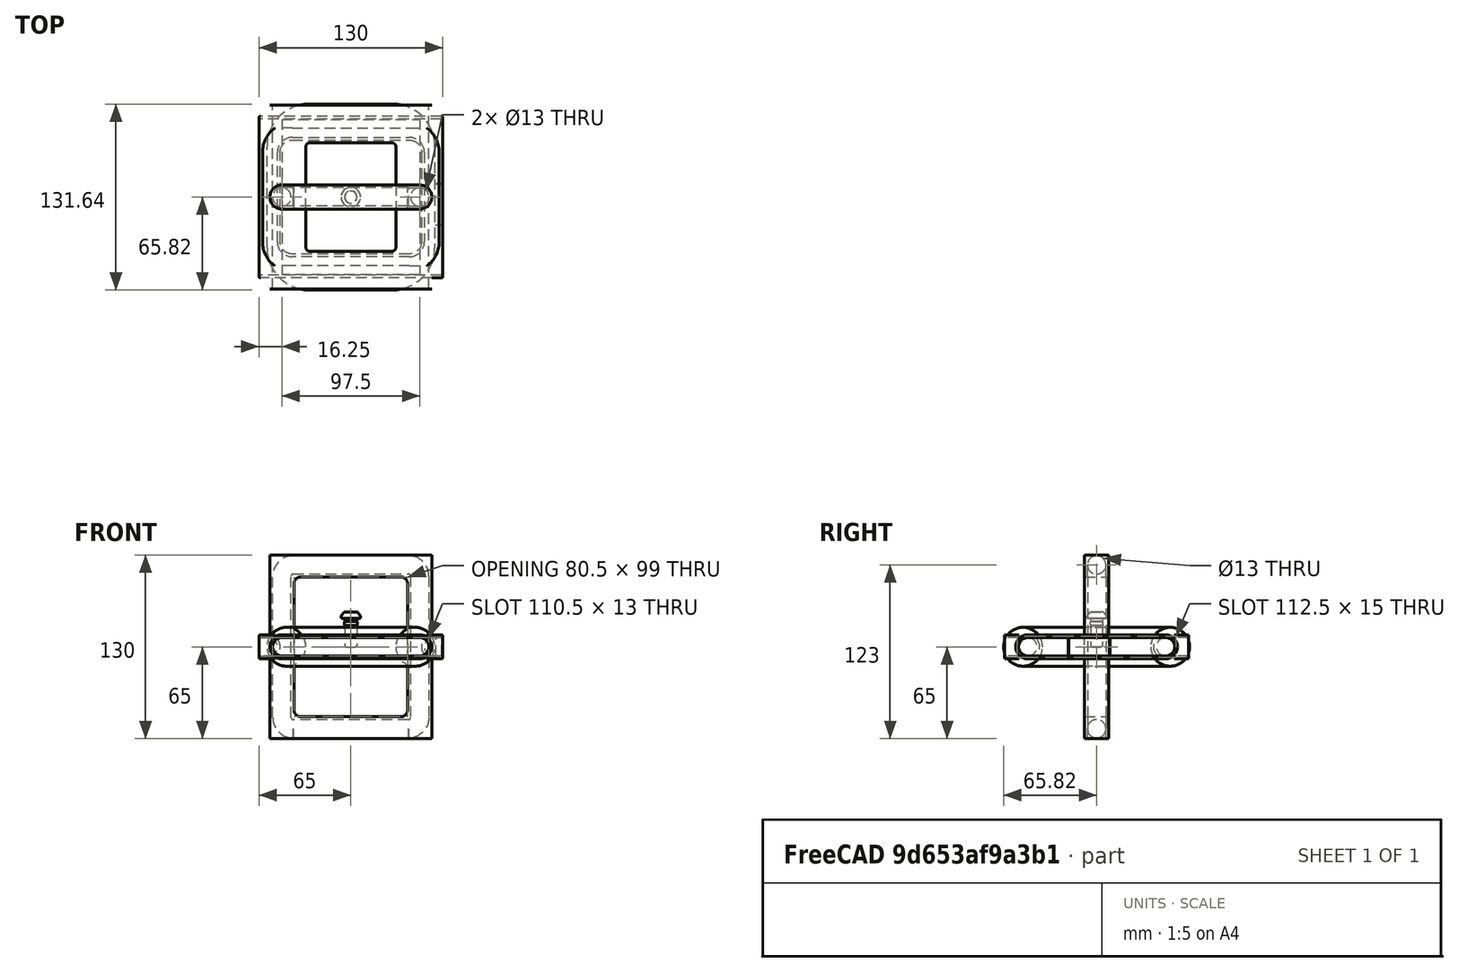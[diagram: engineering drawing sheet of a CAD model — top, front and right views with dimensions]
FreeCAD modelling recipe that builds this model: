
FCSTD DOCUMENT  (FreeCAD 0.19R24291 (Git))
Label: Cooler
License: All rights reserved
LicenseURL: http://en.wikipedia.org/wiki/All_rights_reserved
objects: Sketcher::SketchObject×23, PartDesign::Body×6, PartDesign::Pocket×5, PartDesign::Fillet×5, PartDesign::Pad×4, PartDesign::AdditivePipe×2, PartDesign::SubtractivePipe×1, PartDesign::Boolean×1, PartDesign::Revolution×1
note: 66 computed .brp shape members not serialized (recipe doc carries the construction recipe); baked Part::Feature solids carry a one-line shape summary decoded from their .brp

FEATURE [Sketcher::SketchObject] Sketch
  FullyConstrained = true
  MapMode = 5
  Support = -> [XY_Plane]
  sketch-geometry (6):
    g0: ArcOfCircle CenterX=-48.75 CenterY=-2e-16 CenterZ=0 NormalX=0 NormalY=0 NormalZ=1 AngleXU=0 Radius=8.5 StartAngle=1.5708 EndAngle=4.71239
    g1: ArcOfCircle CenterX=48.75 CenterY=2e-16 CenterZ=0 NormalX=0 NormalY=0 NormalZ=1 AngleXU=0 Radius=8.5 StartAngle=4.71239 EndAngle=7.85398
    g2: LineSegment StartX=-48.75 StartY=-8.5 StartZ=0 EndX=48.75 EndY=-8.5 EndZ=0
    g3: LineSegment StartX=-48.75 StartY=8.5 StartZ=0 EndX=48.75 EndY=8.5 EndZ=0
    g4: LineSegment StartX=48.75 StartY=2e-16 StartZ=0 EndX=57.25 EndY=2e-16 EndZ=0
    g5: LineSegment StartX=-48.75 StartY=-2e-16 StartZ=0 EndX=-57.25 EndY=-2e-16 EndZ=0
  constraints (15):
    c: Tangent(g0,g3) = 1.5708
    c: Tangent(g0,g2) = -1.5708
    c: Tangent(g2,g1) = -1.5708
    c: Tangent(g3,g1) = 1.5708
    c: Horizontal(g2)
    c: Equal(g0,g1)
    c: DistanceY(g0,g0) = 17
    c: Symmetric(g0,g1,g-1)
    c: Coincident(g4,g1)
    c: PointOnObject(g4,g1)
    c: Horizontal(g4)
    c: Coincident(g5,g0)
    c: PointOnObject(g5,g0)
    c: Horizontal(g5)
    c: DistanceX(g5,g4) = 114.5
FEATURE [PartDesign::Pad] Pad
  Direction = (1,1,1)
  Length = 130
  Length2 = 100
  Midplane = true
  Profile = -> Sketch
  Type = 0
FEATURE [Sketcher::SketchObject] Sketch001
  FullyConstrained = true
  MapMode = 5
  Placement = pos=(0,-8.5,0) rot=(1,0,0;1.5708rad)
  Support = -> [Pad]
  sketch-geometry (10):
    g0: LineSegment StartX=-35.25 StartY=49.5 StartZ=0 EndX=35.25 EndY=49.5 EndZ=0
    g1: LineSegment StartX=40.25 StartY=44.5 StartZ=0 EndX=40.25 EndY=-44.5 EndZ=0
    g2: LineSegment StartX=35.25 StartY=-49.5 StartZ=0 EndX=-35.25 EndY=-49.5 EndZ=0
    g3: LineSegment StartX=-40.25 StartY=-44.5 StartZ=0 EndX=-40.25 EndY=44.5 EndZ=0
    g4: LineSegment StartX=-57.25 StartY=0 StartZ=0 EndX=57.25 EndY=0 EndZ=0
    g5: LineSegment StartX=0 StartY=65 StartZ=0 EndX=0 EndY=-65 EndZ=0
    g6: ArcOfCircle CenterX=-35.25 CenterY=44.5 CenterZ=0 NormalX=0 NormalY=0 NormalZ=1 AngleXU=0 Radius=5 StartAngle=1.5708 EndAngle=3.14159
    g7: ArcOfCircle CenterX=-35.25 CenterY=-44.5 CenterZ=0 NormalX=0 NormalY=0 NormalZ=1 AngleXU=0 Radius=5 StartAngle=3.14159 EndAngle=4.71239
    g8: ArcOfCircle CenterX=35.25 CenterY=-44.5 CenterZ=0 NormalX=0 NormalY=0 NormalZ=1 AngleXU=0 Radius=5 StartAngle=4.71239 EndAngle=6.28319
    g9: ArcOfCircle CenterX=35.25 CenterY=44.5 CenterZ=0 NormalX=0 NormalY=0 NormalZ=1 AngleXU=0 Radius=5 StartAngle=0 EndAngle=1.5708
  constraints (25):
    c: Horizontal(g0)
    c: Horizontal(g2)
    c: Vertical(g1)
    c: Vertical(g3)
    c: PointOnObject(g4,g-1)
    c: DistanceX(g4,g4) = 114.5
    c: Symmetric(g4,g4,g-1)
    c: PointOnObject(g5,g-2)
    c: DistanceY(g5,g5) = 130
    c: Symmetric(g5,g5,g-1)
    c: Tangent(g0,g6) = 1.5708
    c: Tangent(g3,g6) = 1.5708
    c: Tangent(g3,g7) = 1.5708
    c: Tangent(g2,g7) = 1.5708
    c: Tangent(g1,g8) = 1.5708
    c: Tangent(g2,g8) = 1.5708
    c: Tangent(g1,g9) = 1.5708
    c: Tangent(g0,g9) = 1.5708
    c: DistanceY(g0,g5) = 15.5
    c: DistanceX(g1,g4) = 17
    c: Symmetric(g6,g8,g-1)
    c: Equal(g9,g6)
    c: Equal(g6,g7)
    c: Equal(g7,g8)
    c: Radius(g7) = 5
FEATURE [PartDesign::Pocket] Pocket
  BaseFeature = -> Pad
  Length = 5
  Length2 = 100
  Profile = -> Sketch001
  Type = 1
FEATURE [Sketcher::SketchObject] Sketch002
  ExternalGeometry = -> [Pocket]
  FullyConstrained = true
  MapMode = 5
  Support = -> [XY_Plane]
  sketch-geometry (4):
    g0: LineSegment StartX=-48.75 StartY=-2e-16 StartZ=0 EndX=48.75 EndY=8.11e-14 EndZ=0
    g1: Circle CenterX=48.75 CenterY=8.11e-14 CenterZ=0 NormalX=0 NormalY=0 NormalZ=1 AngleXU=0 Radius=6.5
    g2: Circle CenterX=-48.75 CenterY=-2e-16 CenterZ=0 NormalX=0 NormalY=0 NormalZ=1 AngleXU=0 Radius=6.5
    g3: LineSegment StartX=-48.75 StartY=-6.5 StartZ=0 EndX=-48.75 EndY=-8.5 EndZ=0
  constraints (9):
    c: Coincident(g0,g-3)
    c: Symmetric(g0,g0,g-1)
    c: Coincident(g1,g0)
    c: Coincident(g2,g0)
    c: Equal(g1,g2)
    c: PointOnObject(g3,g2)
    c: Coincident(g3,g-3)
    c: Vertical(g3)
    c: DistanceY(g3,g3) = 2
FEATURE [Sketcher::SketchObject] Sketch004
  ExternalGeometry = -> [Pocket]
  FullyConstrained = true
  MapMode = 5
  Placement = pos=(0,0,-65) rot=(1,0,0;3.14159rad)
  Support = -> [Pocket]
  sketch-geometry (4):
    g0: ArcOfCircle CenterX=-48.75 CenterY=4.25e-14 CenterZ=0 NormalX=0 NormalY=0 NormalZ=1 AngleXU=0 Radius=6.5 StartAngle=1.5708 EndAngle=4.71239
    g1: ArcOfCircle CenterX=48.75 CenterY=-4.25e-14 CenterZ=0 NormalX=0 NormalY=0 NormalZ=1 AngleXU=0 Radius=6.5 StartAngle=4.71239 EndAngle=7.85398
    g2: LineSegment StartX=-48.75 StartY=-6.5 StartZ=0 EndX=48.75 EndY=-6.5 EndZ=0
    g3: LineSegment StartX=-48.75 StartY=6.5 StartZ=0 EndX=48.75 EndY=6.5 EndZ=0
  constraints (11):
    c: Tangent(g0,g3) = 1.5708
    c: Tangent(g0,g2) = -1.5708
    c: Tangent(g2,g1) = -1.5708
    c: Tangent(g3,g1) = 1.5708
    c: Horizontal(g2)
    c: Symmetric(g1,g0,g-1)
    c: DistanceY(g-3,g0) = 2
    c: Horizontal(g3)
    c: Vertical(g-3,g0)
    c: DistanceY(g1,g1) = 13
    c: DistanceY(g-3,g-4) = 17
FEATURE [Sketcher::SketchObject] Sketch005
  FullyConstrained = false
  MapMode = 5
  Placement = pos=(0,0,0) rot=(1,0,0;1.5708rad)
  Support = -> [XZ_Plane001]
  sketch-geometry (1):
    g0: Circle CenterX=-45.5792 CenterY=0 CenterZ=0 NormalX=0 NormalY=0 NormalZ=1 AngleXU=0 Radius=13.7562
  constraints (1):
    c: PointOnObject(g0,g-1)
FEATURE [Sketcher::SketchObject] Sketch006
  FullyConstrained = false
  MapMode = 5
  Support = -> [XY_Plane001]
  sketch-geometry (8):
    g0: LineSegment StartX=-29.3214 StartY=54.1567 StartZ=0 EndX=29.3214 EndY=54.1567 EndZ=0
    g1: LineSegment StartX=47.6711 StartY=35.807 StartZ=0 EndX=47.6711 EndY=-35.807 EndZ=0
    g2: LineSegment StartX=29.3214 StartY=-54.1567 StartZ=0 EndX=-29.3214 EndY=-54.1567 EndZ=0
    g3: LineSegment StartX=-47.6711 StartY=-35.807 StartZ=0 EndX=-47.6711 EndY=35.807 EndZ=0
    g4: ArcOfCircle CenterX=-29.3214 CenterY=35.807 CenterZ=0 NormalX=0 NormalY=0 NormalZ=1 AngleXU=0 Radius=18.3497 StartAngle=1.5708 EndAngle=3.14159
    g5: ArcOfCircle CenterX=-29.3214 CenterY=-35.807 CenterZ=0 NormalX=0 NormalY=0 NormalZ=1 AngleXU=0 Radius=18.3497 StartAngle=3.14159 EndAngle=4.71239
    g6: ArcOfCircle CenterX=29.3214 CenterY=-35.807 CenterZ=0 NormalX=0 NormalY=0 NormalZ=1 AngleXU=0 Radius=18.3497 StartAngle=4.71239 EndAngle=6.28319
    g7: ArcOfCircle CenterX=29.3214 CenterY=35.807 CenterZ=0 NormalX=0 NormalY=0 NormalZ=1 AngleXU=0 Radius=18.3497 StartAngle=0 EndAngle=1.5708
  constraints (16):
    c: Horizontal(g0)
    c: Horizontal(g2)
    c: Vertical(g1)
    c: Vertical(g3)
    c: Tangent(g0,g4) = 1.5708
    c: Tangent(g3,g4) = 1.5708
    c: Tangent(g3,g5) = 1.5708
    c: Tangent(g2,g5) = 1.5708
    c: Tangent(g2,g6) = 1.5708
    c: Tangent(g1,g6) = 1.5708
    c: Tangent(g1,g7) = 1.5708
    c: Tangent(g0,g7) = 1.5708
    c: Equal(g7,g4)
    c: Equal(g4,g5)
    c: Equal(g5,g6)
    c: Symmetric(g4,g6,g-1)
FEATURE [PartDesign::AdditivePipe] AdditivePipe
  AuxilleryCurvelinear = true
  AuxillerySpineTangent = false
  Binormal = (0,0,0)
  Mode = 0
  Placement = pos=(0,0,0) rot=(1,0,0;1.5708rad)
  Profile = -> Sketch005
  Spine = -> Sketch006
  SpineTangent = false
  Transformation = 0
  Transition = 0
FEATURE [PartDesign::Body] Body001
  Group = -> [Sketch005,Sketch006,AdditivePipe]
  Origin = -> Origin001
  Tip = -> AdditivePipe
FEATURE [Sketcher::SketchObject] Sketch007
  ExternalGeometry = -> [Pocket]
  FullyConstrained = true
  MapMode = 5
  Support = -> [XY_Plane]
  sketch-geometry (2):
    g0: Circle CenterX=-48.75 CenterY=0 CenterZ=0 NormalX=0 NormalY=0 NormalZ=1 AngleXU=0 Radius=6.5
    g1: LineSegment StartX=-57.25 StartY=0 StartZ=0 EndX=-55.25 EndY=0 EndZ=0
  constraints (8):
    c: Radius(g0) = 6.5
    c: PointOnObject(g0,g-1)
    c: PointOnObject(g1,g-3)
    c: PointOnObject(g1,g0)
    c: Horizontal(g1)
    c: PointOnObject(g1,g-1)
    c: DistanceX(g1,g1) = 2
    c: DistanceX(g1,g0) = 8.5
FEATURE [Sketcher::SketchObject] Sketch008
  ExternalGeometry = -> [Pocket]
  FullyConstrained = true
  MapMode = 5
  Placement = pos=(0,0,0) rot=(1,0,0;1.5708rad)
  Support = -> [XZ_Plane]
  sketch-geometry (8):
    g0: LineSegment StartX=-40.75 StartY=58 StartZ=0 EndX=40.75 EndY=58 EndZ=0
    g1: LineSegment StartX=48.75 StartY=50 StartZ=0 EndX=48.75 EndY=-50 EndZ=0
    g2: LineSegment StartX=40.75 StartY=-58 StartZ=0 EndX=-40.75 EndY=-58 EndZ=0
    g3: LineSegment StartX=-48.75 StartY=-50 StartZ=0 EndX=-48.75 EndY=50 EndZ=0
    g4: ArcOfCircle CenterX=-40.75 CenterY=-50 CenterZ=0 NormalX=0 NormalY=0 NormalZ=1 AngleXU=0 Radius=8 StartAngle=3.14159 EndAngle=4.71239
    g5: ArcOfCircle CenterX=40.75 CenterY=-50 CenterZ=0 NormalX=0 NormalY=0 NormalZ=1 AngleXU=0 Radius=8 StartAngle=4.71239 EndAngle=6.28319
    g6: ArcOfCircle CenterX=40.75 CenterY=50 CenterZ=0 NormalX=0 NormalY=0 NormalZ=1 AngleXU=0 Radius=8 StartAngle=0 EndAngle=1.5708
    g7: ArcOfCircle CenterX=-40.75 CenterY=50 CenterZ=0 NormalX=0 NormalY=0 NormalZ=1 AngleXU=0 Radius=8 StartAngle=1.5708 EndAngle=3.14159
  constraints (22):
    c: Horizontal(g0)
    c: Horizontal(g2)
    c: Vertical(g1)
    c: Vertical(g3)
    c: Tangent(g2,g4) = 1.5708
    c: Tangent(g3,g4) = 1.5708
    c: Tangent(g1,g5) = 1.5708
    c: Tangent(g2,g5) = 1.5708
    c: Tangent(g1,g6) = 1.5708
    c: Tangent(g0,g6) = 1.5708
    c: Tangent(g0,g7) = 1.5708
    c: Tangent(g3,g7) = 1.5708
    c: Equal(g7,g6)
    c: Equal(g6,g5)
    c: Equal(g5,g4)
    c: Symmetric(g7,g5,g-1)
    c: DistanceX(g-4,g-1) = 48.75
    c: DistanceY(g-5,g-4) = 15.5
    c: DistanceY(g-5,g0) = 8.5
    c: Radius(g6) = 8
    c: DistanceX(g-4,g-3) = 8.5
    c: Vertical(g3,g-4)
FEATURE [PartDesign::SubtractivePipe] SubtractivePipe
  AuxilleryCurvelinear = true
  AuxillerySpineTangent = false
  BaseFeature = -> Pocket
  Binormal = (0,0,0)
  Mode = 0
  Profile = -> Sketch007
  Spine = -> Sketch008
  SpineTangent = false
  Transformation = 0
  Transition = 1
FEATURE [Sketcher::SketchObject] Sketch003
  ExternalGeometry = -> [SubtractivePipe]
  FullyConstrained = true
  MapMode = 5
  Placement = pos=(0,0,0) rot=(0.57735,0.57735,0.57735;2.0944rad)
  Support = -> [YZ_Plane]
  sketch-geometry (4):
    g0: LineSegment StartX=-6.5 StartY=-65 StartZ=0 EndX=6.5 EndY=-65 EndZ=0
    g1: LineSegment StartX=-6.5 StartY=-65 StartZ=0 EndX=-6.5 EndY=-58 EndZ=0
    g2: LineSegment StartX=6.5 StartY=-65 StartZ=0 EndX=6.5 EndY=-58 EndZ=0
    g3: ArcOfCircle CenterX=3.48e-14 CenterY=-58 CenterZ=0 NormalX=0 NormalY=0 NormalZ=1 AngleXU=0 Radius=6.5 StartAngle=-1.07e-14 EndAngle=3.14159
  constraints (9):
    c: Symmetric(g0,g0,g-2)
    c: Coincident(g0,g1)
    c: Vertical(g1)
    c: Coincident(g0,g2)
    c: Tangent(g3,g2) = -1.5708
    c: Tangent(g1,g3) = 1.5708
    c: Radius(g3) = 6.5
    c: Coincident(g3,g-3)
    c: PointOnObject(g0,g-4)
FEATURE [Sketcher::SketchObject] Sketch009
  FullyConstrained = true
  MapMode = 5
  Placement = pos=(0,0,0) rot=(1,0,0;1.5708rad)
  Support = -> [XZ_Plane002]
  sketch-geometry (10):
    g0: ArcOfCircle CenterX=-48.75 CenterY=0 CenterZ=0 NormalX=0 NormalY=0 NormalZ=1 AngleXU=0 Radius=6.5 StartAngle=1.5708 EndAngle=4.71239
    g1: ArcOfCircle CenterX=48.75 CenterY=0 CenterZ=0 NormalX=0 NormalY=0 NormalZ=1 AngleXU=0 Radius=6.5 StartAngle=4.71239 EndAngle=7.85398
    g2: LineSegment StartX=-48.75 StartY=-6.5 StartZ=0 EndX=48.75 EndY=-6.5 EndZ=0
    g3: LineSegment StartX=-48.75 StartY=6.5 StartZ=0 EndX=48.75 EndY=6.5 EndZ=0
    g4: ArcOfCircle CenterX=-48.75 CenterY=0 CenterZ=0 NormalX=0 NormalY=0 NormalZ=1 AngleXU=0 Radius=8.5 StartAngle=1.5708 EndAngle=4.71239
    g5: ArcOfCircle CenterX=48.75 CenterY=0 CenterZ=0 NormalX=0 NormalY=0 NormalZ=1 AngleXU=0 Radius=8.5 StartAngle=4.71239 EndAngle=7.85398
    g6: LineSegment StartX=-48.75 StartY=-8.5 StartZ=0 EndX=48.75 EndY=-8.5 EndZ=0
    g7: LineSegment StartX=-48.75 StartY=8.5 StartZ=0 EndX=48.75 EndY=8.5 EndZ=0
    g8: LineSegment StartX=48.75 StartY=0 StartZ=0 EndX=57.25 EndY=0 EndZ=0
    g9: LineSegment StartX=-48.75 StartY=0 StartZ=0 EndX=-57.25 EndY=0 EndZ=0
  constraints (23):
    c: Tangent(g0,g3) = 1.5708
    c: Tangent(g0,g2) = -1.5708
    c: Tangent(g2,g1) = -1.5708
    c: Tangent(g3,g1) = 1.5708
    c: Horizontal(g2)
    c: Tangent(g4,g7) = 1.5708
    c: Tangent(g4,g6) = -1.5708
    c: Tangent(g6,g5) = -1.5708
    c: Tangent(g7,g5) = 1.5708
    c: Horizontal(g6)
    c: Coincident(g4,g0)
    c: Coincident(g1,g5)
    c: DistanceY(g1,g5) = 2
    c: Symmetric(g0,g1,g-2)
    c: PointOnObject(g0,g-1)
    c: Radius(g4) = 8.5
    c: Coincident(g8,g1)
    c: PointOnObject(g8,g-1)
    c: PointOnObject(g8,g5)
    c: Coincident(g9,g0)
    c: PointOnObject(g9,g-1)
    c: PointOnObject(g9,g4)
    c: DistanceX(g9,g8) = 114.5
FEATURE [Sketcher::SketchObject] Sketch010
  ExternalGeometry = -> [Sketch009]
  FullyConstrained = true
  MapMode = 5
  Placement = pos=(0,0,0) rot=(1,0,0;1.5708rad)
  Support = -> [XZ_Plane002]
  sketch-geometry (6):
    g0: Circle CenterX=-48.75 CenterY=0 CenterZ=0 NormalX=0 NormalY=0 NormalZ=1 AngleXU=0 Radius=8.5
    g1: Circle CenterX=-48.75 CenterY=0 CenterZ=0 NormalX=0 NormalY=0 NormalZ=1 AngleXU=0 Radius=6.5
    g2: LineSegment StartX=-55.25 StartY=0 StartZ=0 EndX=-57.25 EndY=0 EndZ=0
    g3: Circle CenterX=48.75 CenterY=0 CenterZ=0 NormalX=0 NormalY=0 NormalZ=1 AngleXU=0 Radius=6.5
    g4: Circle CenterX=48.75 CenterY=0 CenterZ=0 NormalX=0 NormalY=0 NormalZ=1 AngleXU=0 Radius=8.5
    g5: LineSegment StartX=55.25 StartY=0 StartZ=0 EndX=57.25 EndY=0 EndZ=0
  constraints (16):
    c: Coincident(g0,g-3)
    c: Coincident(g1,g0)
    c: PointOnObject(g2,g1)
    c: PointOnObject(g2,g0)
    c: Horizontal(g2)
    c: DistanceX(g2,g2) = 2
    c: PointOnObject(g2,g-1)
    c: Coincident(g4,g3)
    c: PointOnObject(g5,g3)
    c: PointOnObject(g5,g4)
    c: Horizontal(g5)
    c: Equal(g5,g2)
    c: Equal(g4,g0)
    c: Symmetric(g3,g0,g-1)
    c: PointOnObject(g5,g-1)
    c: Equal(g0,g-3)
FEATURE [PartDesign::Pad] Pad001
  Direction = (1,1,1)
  Length = 130
  Length2 = 100
  Midplane = true
  Placement = pos=(0,0,0) rot=(1,0,0;1.5708rad)
  Profile = -> Sketch009
  Type = 0
FEATURE [Sketcher::SketchObject] Sketch011
  ExternalGeometry = -> [Pad001]
  FullyConstrained = true
  MapMode = 5
  Placement = pos=(0,3.7e-15,8.5) rot=(0,0,1;3.14159rad)
  Support = -> [Pad001]
  sketch-geometry (4):
    g0: LineSegment StartX=-48.75 StartY=55 StartZ=0 EndX=48.75 EndY=55 EndZ=0
    g1: LineSegment StartX=48.75 StartY=55 StartZ=0 EndX=48.75 EndY=-55 EndZ=0
    g2: LineSegment StartX=48.75 StartY=-55 StartZ=0 EndX=-48.75 EndY=-55 EndZ=0
    g3: LineSegment StartX=-48.75 StartY=-55 StartZ=0 EndX=-48.75 EndY=55 EndZ=0
  constraints (11):
    c: Coincident(g0,g1)
    c: Coincident(g1,g2)
    c: Coincident(g2,g3)
    c: Coincident(g3,g0)
    c: Horizontal(g0)
    c: Vertical(g3)
    c: Symmetric(g2,g1,g-2)
    c: Symmetric(g0,g1,g-1)
    c: PointOnObject(g0,g-3)
    c: DistanceY(g2,g-1) = 55
    c: DistanceX(g0,g0) = 97.5
FEATURE [PartDesign::Pocket] Pocket003
  BaseFeature = -> Pad001
  Length = 5
  Length2 = 100
  Placement = pos=(0,0,0) rot=(1,0,0;1.5708rad)
  Profile = -> Sketch011
  Type = 1
FEATURE [Sketcher::SketchObject] Sketch012
  FullyConstrained = false
  MapMode = 2
  Placement = pos=(0,0,0) rot=(0.57735,0.57735,0.57735;2.0944rad)
  Support = -> [YZ_Plane002]
  sketch-geometry (8):
    g0: LineSegment StartX=-65 StartY=8.5 StartZ=0 EndX=-55 EndY=8.5 EndZ=0
    g1: LineSegment StartX=-65 StartY=-8.5 StartZ=0 EndX=-55 EndY=-8.5 EndZ=0
    g2: ArcOfCircle CenterX=-55 CenterY=6.95e-14 CenterZ=0 NormalX=0 NormalY=0 NormalZ=1 AngleXU=0 Radius=8.5 StartAngle=4.71239 EndAngle=7.85398
    g3: ArcOfCircle CenterX=-55 CenterY=6.95e-14 CenterZ=0 NormalX=0 NormalY=0 NormalZ=1 AngleXU=0 Radius=6.5 StartAngle=4.71239 EndAngle=7.85398
    g4: LineSegment StartX=-65 StartY=8.5 StartZ=0 EndX=-65 EndY=6.5 EndZ=0
    g5: LineSegment StartX=-65 StartY=6.5 StartZ=0 EndX=-55 EndY=6.5 EndZ=0
    g6: LineSegment StartX=-55 StartY=-6.5 StartZ=0 EndX=-65 EndY=-6.5 EndZ=0
    g7: LineSegment StartX=-65 StartY=-6.5 StartZ=0 EndX=-65 EndY=-8.5 EndZ=0
  constraints (16):
    c: Tangent(g2,g1) = -1.5708
    c: Tangent(g0,g2) = 1.5708
    c: Horizontal(g0)
    c: Horizontal(g1)
    c: Coincident(g3,g2)
    c: DistanceY(g3,g0) = 2
    c: Coincident(g0,g4)
    c: Vertical(g4)
    c: Coincident(g4,g5)
    c: Horizontal(g5)
    c: Tangent(g3,g6) = 1.5708
    c: Coincident(g6,g7)
    c: Coincident(g7,g1)
    c: Vertical(g7)
    c: Horizontal(g6)
    c: Tangent(g5,g3) = 1.5708
FEATURE [Sketcher::SketchObject] Sketch013
  FullyConstrained = false
  MapMode = 2
  Placement = pos=(0,0,0) rot=(0.57735,0.57735,0.57735;2.0944rad)
  Support = -> [YZ_Plane002]
  sketch-geometry (4):
    g0: ArcOfCircle CenterX=-55 CenterY=0 CenterZ=0 NormalX=0 NormalY=0 NormalZ=1 AngleXU=0 Radius=6.5 StartAngle=4.71239 EndAngle=7.85398
    g1: LineSegment StartX=-65 StartY=-6.5 StartZ=0 EndX=-65 EndY=6.5 EndZ=0
    g2: LineSegment StartX=-65 StartY=6.5 StartZ=0 EndX=-55 EndY=6.5 EndZ=0
    g3: LineSegment StartX=-55 StartY=-6.5 StartZ=0 EndX=-65 EndY=-6.5 EndZ=0
  constraints (9):
    c: Coincident(g1,g2)
    c: Horizontal(g2)
    c: Tangent(g0,g3) = 1.5708
    c: Horizontal(g3)
    c: Tangent(g2,g0) = 1.5708
    c: Coincident(g1,g3)
    c: DistanceX(g2,g2) = 10
    c: Radius(g0) = 6.5
    c: Symmetric(g1,g1,g-1)
FEATURE [Sketcher::SketchObject] Sketch014
  FullyConstrained = false
  MapMode = 5
  Placement = pos=(0,0,0) rot=(1,0,0;1.5708rad)
  Support = -> [XZ_Plane002]
  sketch-geometry (2):
    g0: Circle CenterX=-48.75 CenterY=1.443e-13 CenterZ=0 NormalX=0 NormalY=0 NormalZ=1 AngleXU=0 Radius=6.5
    g1: Circle CenterX=48.75 CenterY=1.443e-13 CenterZ=0 NormalX=0 NormalY=0 NormalZ=1 AngleXU=0 Radius=6.5
  constraints (2):
    c: Equal(g1,g0)
    c: Symmetric(g1,g0,g-2)
FEATURE [PartDesign::Body] Body002
  Group = -> [Sketch009,Sketch010,Pad001,Sketch011,Pocket003,Sketch012,Sketch013,Sketch014]
  Origin = -> Origin002
  Tip = -> Pocket003
FEATURE [PartDesign::Pocket] Pocket006
  BaseFeature = -> SubtractivePipe
  Length = 81.5
  Length2 = 100
  Midplane = true
  Profile = -> Sketch003
  Type = 0
FEATURE [PartDesign::Body] Body
  Group = -> [Sketch,Pad,Sketch001,Pocket,Sketch002,Sketch003,Sketch004,Sketch007,Sketch008,SubtractivePipe,Pocket006]
  Origin = -> Origin
  Tip = -> Pocket006
FEATURE [Sketcher::SketchObject] Sketch015
  FullyConstrained = true
  MapMode = 5
  Support = -> [XY_Plane003]
  sketch-geometry (8):
    g0: LineSegment StartX=-41.5 StartY=40.25 StartZ=0 EndX=41.5 EndY=40.25 EndZ=0
    g1: LineSegment StartX=50 StartY=31.75 StartZ=0 EndX=50 EndY=-31.75 EndZ=0
    g2: LineSegment StartX=41.5 StartY=-40.25 StartZ=0 EndX=-41.5 EndY=-40.25 EndZ=0
    g3: LineSegment StartX=-50 StartY=-31.75 StartZ=0 EndX=-50 EndY=31.75 EndZ=0
    g4: ArcOfCircle CenterX=-41.5 CenterY=-31.75 CenterZ=0 NormalX=0 NormalY=0 NormalZ=1 AngleXU=0 Radius=8.5 StartAngle=3.14159 EndAngle=4.71239
    g5: ArcOfCircle CenterX=41.5 CenterY=-31.75 CenterZ=0 NormalX=0 NormalY=0 NormalZ=1 AngleXU=0 Radius=8.5 StartAngle=4.71239 EndAngle=6.28319
    g6: ArcOfCircle CenterX=41.5 CenterY=31.75 CenterZ=0 NormalX=0 NormalY=0 NormalZ=1 AngleXU=0 Radius=8.5 StartAngle=0 EndAngle=1.5708
    g7: ArcOfCircle CenterX=-41.5 CenterY=31.75 CenterZ=0 NormalX=0 NormalY=0 NormalZ=1 AngleXU=0 Radius=8.5 StartAngle=1.5708 EndAngle=3.14159
  constraints (19):
    c: Horizontal(g0)
    c: Horizontal(g2)
    c: Vertical(g1)
    c: Vertical(g3)
    c: Tangent(g2,g4) = 1.5708
    c: Tangent(g3,g4) = 1.5708
    c: Tangent(g1,g5) = 1.5708
    c: Tangent(g2,g5) = 1.5708
    c: Tangent(g1,g6) = 1.5708
    c: Tangent(g0,g6) = 1.5708
    c: Tangent(g0,g7) = 1.5708
    c: Tangent(g3,g7) = 1.5708
    c: Equal(g7,g6)
    c: Equal(g6,g5)
    c: Equal(g5,g4)
    c: Symmetric(g7,g5,g-1)
    c: Radius(g6) = 8.5
    c: DistanceX(g3,g1) = 100
    c: DistanceY(g2,g0) = 80.5
FEATURE [Sketcher::SketchObject] Sketch016
  ExternalGeometry = -> [Pocket]
  FullyConstrained = true
  MapMode = 5
  Support = -> [XY_Plane003]
  sketch-geometry (2):
    g0: Circle CenterX=-48.75 CenterY=0 CenterZ=0 NormalX=0 NormalY=0 NormalZ=1 AngleXU=0 Radius=6.5
    g1: LineSegment StartX=-57.25 StartY=0 StartZ=0 EndX=-55.25 EndY=0 EndZ=0
  constraints (8):
    c: Radius(g0) = 6.5
    c: PointOnObject(g0,g-1)
    c: PointOnObject(g1,g-3)
    c: PointOnObject(g1,g0)
    c: Horizontal(g1)
    c: PointOnObject(g1,g-1)
    c: DistanceX(g1,g1) = 2
    c: DistanceX(g1,g0) = 8.5
FEATURE [Sketcher::SketchObject] Sketch017
  ExternalGeometry = -> [Sketch015]
  FullyConstrained = true
  MapMode = 2
  Placement = pos=(0,0,0) rot=(0.57735,0.57735,0.57735;2.0944rad)
  Support = -> [YZ_Plane003]
  sketch-geometry (9):
    g0: LineSegment StartX=-52.75 StartY=8.5 StartZ=0 EndX=-48.75 EndY=8.5 EndZ=0
    g1: LineSegment StartX=-52.75 StartY=-8.5 StartZ=0 EndX=-48.75 EndY=-8.5 EndZ=0
    g2: ArcOfCircle CenterX=-48.75 CenterY=0 CenterZ=0 NormalX=0 NormalY=0 NormalZ=1 AngleXU=0 Radius=8.5 StartAngle=4.71239 EndAngle=7.85398
    g3: ArcOfCircle CenterX=-48.75 CenterY=0 CenterZ=0 NormalX=0 NormalY=0 NormalZ=1 AngleXU=0 Radius=6.5 StartAngle=4.71239 EndAngle=7.85398
    g4: LineSegment StartX=-52.75 StartY=8.5 StartZ=0 EndX=-52.75 EndY=6.5 EndZ=0
    g5: LineSegment StartX=-52.75 StartY=6.5 StartZ=0 EndX=-48.75 EndY=6.5 EndZ=0
    g6: LineSegment StartX=-48.75 StartY=-6.5 StartZ=0 EndX=-52.75 EndY=-6.5 EndZ=0
    g7: LineSegment StartX=-52.75 StartY=-6.5 StartZ=0 EndX=-52.75 EndY=-8.5 EndZ=0
    g8: GeomPoint X=-40.25 Y=-1.12e-14 Z=0
  constraints (23):
    c: Tangent(g2,g1) = -1.5708
    c: Tangent(g0,g2) = 1.5708
    c: Horizontal(g0)
    c: Horizontal(g1)
    c: Coincident(g3,g2)
    c: DistanceY(g3,g0) = 2
    c: Coincident(g0,g4)
    c: Vertical(g4)
    c: Coincident(g4,g5)
    c: Horizontal(g5)
    c: Tangent(g3,g6) = 1.5708
    c: Coincident(g6,g7)
    c: Coincident(g7,g1)
    c: Vertical(g7)
    c: Horizontal(g6)
    c: Tangent(g5,g3) = 1.5708
    c: Radius(g2) = 8.5
    c: PointOnObject(g2,g-1)
    c: Vertical(g6,g0)
    c: DistanceX(g1,g1) = 4
    c: PointOnObject(g8,g2)
    c: Coincident(g8,g-3)
    c: DistanceX(g1,g8) = 12.5
FEATURE [PartDesign::AdditivePipe] AdditivePipe001
  AuxilleryCurvelinear = true
  AuxillerySpineTangent = false
  Binormal = (0,0,0)
  Mode = 0
  Placement = pos=(0,0,0) rot=(0.57735,0.57735,0.57735;2.0944rad)
  Profile = -> Sketch017
  Spine = -> Sketch015
  SpineTangent = false
  Transformation = 0
  Transition = 0
FEATURE [Sketcher::SketchObject] Sketch018
  FullyConstrained = true
  MapMode = 5
  Placement = pos=(0,0,0) rot=(0.57735,0.57735,0.57735;2.0944rad)
  Support = -> [YZ_Plane004]
  sketch-geometry (8):
    g0: ArcOfCircle CenterX=-48.75 CenterY=0 CenterZ=0 NormalX=0 NormalY=0 NormalZ=1 AngleXU=0 Radius=6.5 StartAngle=1.5708 EndAngle=4.71239
    g1: ArcOfCircle CenterX=48.75 CenterY=0 CenterZ=0 NormalX=0 NormalY=0 NormalZ=1 AngleXU=0 Radius=6.5 StartAngle=4.71239 EndAngle=7.85398
    g2: LineSegment StartX=-48.75 StartY=-6.5 StartZ=0 EndX=48.75 EndY=-6.5 EndZ=0
    g3: LineSegment StartX=-48.75 StartY=6.5 StartZ=0 EndX=48.75 EndY=6.5 EndZ=0
    g4: ArcOfCircle CenterX=-48.75 CenterY=0 CenterZ=0 NormalX=0 NormalY=0 NormalZ=1 AngleXU=0 Radius=8.5 StartAngle=1.5708 EndAngle=4.71239
    g5: ArcOfCircle CenterX=48.75 CenterY=0 CenterZ=0 NormalX=0 NormalY=0 NormalZ=1 AngleXU=0 Radius=8.5 StartAngle=4.71239 EndAngle=7.85398
    g6: LineSegment StartX=-48.75 StartY=-8.5 StartZ=0 EndX=48.75 EndY=-8.5 EndZ=0
    g7: LineSegment StartX=-48.75 StartY=8.5 StartZ=0 EndX=48.75 EndY=8.5 EndZ=0
  constraints (17):
    c: Tangent(g0,g3) = 1.5708
    c: Tangent(g0,g2) = -1.5708
    c: Tangent(g2,g1) = -1.5708
    c: Tangent(g3,g1) = 1.5708
    c: Horizontal(g2)
    c: PointOnObject(g1,g-1)
    c: Tangent(g4,g7) = 1.5708
    c: Tangent(g4,g6) = -1.5708
    c: Tangent(g6,g5) = -1.5708
    c: Tangent(g7,g5) = 1.5708
    c: Horizontal(g6)
    c: Coincident(g5,g1)
    c: Coincident(g4,g0)
    c: DistanceY(g4,g0) = 2
    c: DistanceY(g5,g5) = 17
    c: DistanceX(g0,g1) = 97.5
    c: Symmetric(g0,g1,g-2)
FEATURE [PartDesign::Pad] Pad002
  Direction = (1,1,1)
  Length = 130
  Length2 = 100
  Midplane = true
  Placement = pos=(0,0,0) rot=(0.57735,0.57735,0.57735;2.0944rad)
  Profile = -> Sketch018
  Type = 0
FEATURE [Sketcher::SketchObject] Sketch019
  FullyConstrained = true
  MapMode = 5
  Placement = pos=(2.4e-15,-3.7e-15,-8.5) rot=(0.707107,0.707107,0;3.14159rad)
  Support = -> [Pad002]
  sketch-geometry (8):
    g0: LineSegment StartX=-40.25 StartY=58.5 StartZ=0 EndX=40.25 EndY=58.5 EndZ=0
    g1: LineSegment StartX=48.75 StartY=50 StartZ=0 EndX=48.75 EndY=-50 EndZ=0
    g2: LineSegment StartX=40.25 StartY=-58.5 StartZ=0 EndX=-40.25 EndY=-58.5 EndZ=0
    g3: LineSegment StartX=-48.75 StartY=-50 StartZ=0 EndX=-48.75 EndY=50 EndZ=0
    g4: ArcOfCircle CenterX=-40.25 CenterY=50 CenterZ=0 NormalX=0 NormalY=0 NormalZ=1 AngleXU=0 Radius=8.5 StartAngle=1.5708 EndAngle=3.14159
    g5: ArcOfCircle CenterX=-40.25 CenterY=-50 CenterZ=0 NormalX=0 NormalY=0 NormalZ=1 AngleXU=0 Radius=8.5 StartAngle=3.14159 EndAngle=4.71239
    g6: ArcOfCircle CenterX=40.25 CenterY=-50 CenterZ=0 NormalX=0 NormalY=0 NormalZ=1 AngleXU=0 Radius=8.5 StartAngle=4.71239 EndAngle=6.28319
    g7: ArcOfCircle CenterX=40.25 CenterY=50 CenterZ=0 NormalX=0 NormalY=0 NormalZ=1 AngleXU=0 Radius=8.5 StartAngle=0 EndAngle=1.5708
  constraints (19):
    c: Horizontal(g0)
    c: Horizontal(g2)
    c: Vertical(g1)
    c: Vertical(g3)
    c: Tangent(g0,g4) = 1.5708
    c: Tangent(g3,g4) = 1.5708
    c: Tangent(g3,g5) = 1.5708
    c: Tangent(g2,g5) = 1.5708
    c: Tangent(g2,g6) = 1.5708
    c: Tangent(g1,g6) = 1.5708
    c: Tangent(g1,g7) = 1.5708
    c: Tangent(g0,g7) = 1.5708
    c: Equal(g4,g7)
    c: Equal(g7,g5)
    c: Equal(g5,g6)
    c: Radius(g7) = 8.5
    c: Symmetric(g4,g6,g-1)
    c: DistanceX(g3,g1) = 97.5
    c: DistanceY(g2,g0) = 117
FEATURE [PartDesign::Pocket] Pocket007
  BaseFeature = -> Pad002
  Length = 5
  Length2 = 100
  Placement = pos=(0,0,0) rot=(0.57735,0.57735,0.57735;2.0944rad)
  Profile = -> Sketch019
  Type = 1
FEATURE [Sketcher::SketchObject] Sketch020
  ExternalGeometry = -> [AdditivePipe001]
  FullyConstrained = true
  MapMode = 5
  Placement = pos=(0,3.7e-15,-8.5) rot=(0.707107,0.707107,0;3.14159rad)
  Support = -> [AdditivePipe001]
  sketch-geometry (8):
    g0: LineSegment StartX=-68.75 StartY=90 StartZ=0 EndX=68.75 EndY=90 EndZ=0
    g1: LineSegment StartX=68.75 StartY=90 StartZ=0 EndX=68.75 EndY=-90 EndZ=0
    g2: LineSegment StartX=68.75 StartY=-90 StartZ=0 EndX=-68.75 EndY=-90 EndZ=0
    g3: LineSegment StartX=-68.75 StartY=-90 StartZ=0 EndX=-68.75 EndY=90 EndZ=0
    g4: LineSegment StartX=-48.75 StartY=80 StartZ=0 EndX=48.75 EndY=80 EndZ=0
    g5: LineSegment StartX=48.75 StartY=80 StartZ=0 EndX=48.75 EndY=-80 EndZ=0
    g6: LineSegment StartX=48.75 StartY=-80 StartZ=0 EndX=-48.75 EndY=-80 EndZ=0
    g7: LineSegment StartX=-48.75 StartY=-80 StartZ=0 EndX=-48.75 EndY=80 EndZ=0
  constraints (20):
    c: Coincident(g0,g1)
    c: Coincident(g1,g2)
    c: Coincident(g2,g3)
    c: Coincident(g3,g0)
    c: Horizontal(g2)
    c: Vertical(g3)
    c: Symmetric(g0,g0,g-2)
    c: Symmetric(g0,g1,g-1)
    c: Coincident(g4,g5)
    c: Coincident(g5,g6)
    c: Coincident(g6,g7)
    c: Coincident(g7,g4)
    c: Horizontal(g4)
    c: Vertical(g7)
    c: Symmetric(g5,g6,g-2)
    c: Symmetric(g4,g5,g-1)
    c: PointOnObject(g-3,g5)
    c: DistanceY(g1,g5) = 10
    c: DistanceX(g2,g6) = 20
    c: DistanceY(g1,g-1) = 90
FEATURE [PartDesign::Pocket] Pocket008
  BaseFeature = -> AdditivePipe001
  Length = 5
  Length2 = 100
  Placement = pos=(0,0,0) rot=(0.57735,0.57735,0.57735;2.0944rad)
  Profile = -> Sketch020
  Type = 1
FEATURE [PartDesign::Body] Body003
  Group = -> [Sketch015,Sketch016,Sketch017,AdditivePipe001,Sketch020,Pocket008]
  Origin = -> Origin003
  Tip = -> Pocket008
FEATURE [PartDesign::Fillet] Fillet
  Base = -> Pocket007 [Edge22,Edge38,Edge21,Edge41]
  BaseFeature = -> Pocket007
  Placement = pos=(0,0,0) rot=(0.57735,0.57735,0.57735;2.0944rad)
  Radius = 0.999
  SupportTransform = false
FEATURE [PartDesign::Boolean] Boolean
  BaseFeature = -> Fillet
  Group = -> [Body003]
  Type = 0
FEATURE [Sketcher::SketchObject] Sketch021
  FullyConstrained = true
  MapMode = 5
  Placement = pos=(0,0,0) rot=(1,0,0;1.5708rad)
  Support = -> [XZ_Plane005]
  sketch-geometry (15):
    g0: LineSegment StartX=0 StartY=0 StartZ=0 EndX=-4.2 EndY=0 EndZ=0
    g1: LineSegment StartX=-4.2 StartY=0 StartZ=0 EndX=-4.2 EndY=15.7 EndZ=0
    g2: LineSegment StartX=-4.2 StartY=15.7 StartZ=0 EndX=-4.5 EndY=15.7 EndZ=0
    g3: LineSegment StartX=-4.5 StartY=15.7 StartZ=0 EndX=-4.5 EndY=17.5 EndZ=0
    g4: LineSegment StartX=-4.5 StartY=17.5 StartZ=0 EndX=-4.2 EndY=17.5 EndZ=0
    g5: LineSegment StartX=-4.2 StartY=17.5 StartZ=0 EndX=-4.2 EndY=20.2 EndZ=0
    g6: LineSegment StartX=-4.2 StartY=20.2 StartZ=0 EndX=-6.9 EndY=20.2 EndZ=0
    g7: LineSegment StartX=0 StartY=0 StartZ=0 EndX=0 EndY=24.5 EndZ=0
    g8: LineSegment StartX=-6.9 StartY=20.2 StartZ=0 EndX=-6.9 EndY=21.9 EndZ=0
    g9: LineSegment StartX=-4.5 StartY=15.7 StartZ=0 EndX=-4.2 EndY=15.1804 EndZ=0
    g10: LineSegment StartX=-4.2 StartY=15.1804 StartZ=0 EndX=-4.2 EndY=0 EndZ=0
    g11: LineSegment StartX=0 StartY=24.5 StartZ=0 EndX=-4.75 EndY=24.5 EndZ=0
    g12: LineSegment StartX=-4.75 StartY=24.5 StartZ=0 EndX=-6.9 EndY=21.9 EndZ=0
    g13: LineSegment StartX=-4.5 StartY=17.5 StartZ=0 EndX=-4.2 EndY=18.0196 EndZ=0
    g14: LineSegment StartX=-4.2 StartY=20.2 StartZ=0 EndX=-4.2 EndY=18.0196 EndZ=0
  constraints (44):
    c: Horizontal(g0)
    c: Coincident(g0,g1)
    c: Vertical(g1)
    c: Coincident(g1,g2)
    c: Coincident(g2,g3)
    c: Coincident(g3,g4)
    c: Coincident(g4,g5)
    c: Vertical(g5)
    c: Coincident(g5,g6)
    c: Coincident(g0,g7)
    c: Vertical(g7)
    c: DistanceX(g0,g0) = 4.2
    c: Horizontal(g2)
    c: Vertical(g3)
    c: DistanceY(g3,g3) = 1.8
    c: Horizontal(g4)
    c: Vertical(g4,g1)
    c: DistanceX(g2,g2) = 0.3
    c: DistanceY(g1,g1) = 15.7
    c: DistanceY(g5,g5) = 2.7
    c: Horizontal(g6)
    c: Equal(g5,g6)
    c: PointOnObject(g7,g-2)
    c: PointOnObject(g0,g-1)
    c: Coincident(g8,g6)
    c: DistanceY(g8,g8) = 1.7
    c: DistanceY(g7,g7) = 24.5
    c: Vertical(g8)
    c: Coincident(g9,g2)
    c: PointOnObject(g9,g1)
    c: Coincident(g10,g9)
    c: Coincident(g10,g0)
    c: Angle(g9,g2) = 1.0472
    c: Coincident(g7,g11)
    c: Horizontal(g11)
    c: Coincident(g11,g12)
    c: Coincident(g12,g8)
    c: DistanceX(g11,g11) = 4.75
    c: Coincident(g13,g3)
    c: PointOnObject(g13,g5)
    c: Equal(g9,g13)
    c: Coincident(g14,g6)
    c: Coincident(g14,g13)
    c: Angle(g12,g11) = 2.26174
FEATURE [PartDesign::Revolution] Revolution
  Angle = 360
  Axis = (0,-2e-16,1)
  Base = (0,0,0)
  Placement = pos=(0,0,0) rot=(1,0,0;1.5708rad)
  Profile = -> Sketch021
  ReferenceAxis = -> Sketch021 [V_Axis]
FEATURE [PartDesign::Fillet] Fillet001
  Base = -> Revolution [Edge1]
  BaseFeature = -> Revolution
  Placement = pos=(0,0,0) rot=(1,0,0;1.5708rad)
  Radius = 1
  SupportTransform = false
FEATURE [PartDesign::Fillet] Fillet002
  Base = -> Fillet001 [Edge6]
  BaseFeature = -> Fillet001
  Placement = pos=(0,0,0) rot=(1,0,0;1.5708rad)
  Radius = 1
  SupportTransform = false
FEATURE [PartDesign::Fillet] Fillet003
  Base = -> Fillet002 [Edge9]
  BaseFeature = -> Fillet002
  Placement = pos=(0,0,0) rot=(1,0,0;1.5708rad)
  Radius = 1
  SupportTransform = false
FEATURE [PartDesign::Fillet] Fillet004
  Base = -> Fillet003 [Edge21,Edge19]
  BaseFeature = -> Fillet003
  Placement = pos=(0,0,0) rot=(1,0,0;1.5708rad)
  Radius = 1
  SupportTransform = false
FEATURE [PartDesign::Body] Body005  label="Pin"
  Group = -> [Sketch021,Revolution,Fillet001,Fillet002,Fillet003,Fillet004]
  Origin = -> Origin005
  Tip = -> Fillet004
FEATURE [Sketcher::SketchObject] Sketch022
  ExternalGeometry = -> [Boolean]
  FullyConstrained = false
  MapMode = 5
  Placement = pos=(1.8e-15,-2.9e-15,-6.5) rot=(0,0,1;0rad)
  Support = -> [Boolean]
  sketch-geometry (8):
    g0: LineSegment StartX=64.301 StartY=9.55412 StartZ=0 EndX=60.301 EndY=9.55412 EndZ=0
    g1: LineSegment StartX=60.301 StartY=9.55412 StartZ=0 EndX=60.301 EndY=9.25412 EndZ=0
    g2: LineSegment StartX=60.301 StartY=9.25412 StartZ=0 EndX=64.301 EndY=9.25412 EndZ=0
    g3: LineSegment StartX=64.301 StartY=9.25412 StartZ=0 EndX=64.301 EndY=9.55412 EndZ=0
    g4: LineSegment StartX=60.301 StartY=-19.6785 StartZ=0 EndX=64.301 EndY=-19.6785 EndZ=0
    g5: LineSegment StartX=64.301 StartY=-19.6785 StartZ=0 EndX=64.301 EndY=-19.9785 EndZ=0
    g6: LineSegment StartX=64.301 StartY=-19.9785 StartZ=0 EndX=60.301 EndY=-19.9785 EndZ=0
    g7: LineSegment StartX=60.301 StartY=-19.9785 StartZ=0 EndX=60.301 EndY=-19.6785 EndZ=0
  constraints (22):
    c: Coincident(g0,g1)
    c: Coincident(g1,g2)
    c: Coincident(g2,g3)
    c: Coincident(g3,g0)
    c: Horizontal(g0)
    c: Horizontal(g2)
    c: Vertical(g1)
    c: Vertical(g3)
    c: DistanceY(g3,g3) = 0.3
    c: DistanceX(g0,g0) = 4
    c: Coincident(g4,g5)
    c: Coincident(g5,g6)
    c: Coincident(g6,g7)
    c: Coincident(g7,g4)
    c: Horizontal(g4)
    c: Horizontal(g6)
    c: Vertical(g5)
    c: Vertical(g7)
    c: Equal(g0,g4)
    c: Equal(g3,g5)
    c: DistanceX(g-3,g5) = 0.3
    c: Vertical(g2,g4)
FEATURE [PartDesign::Pad] Pad003
  BaseFeature = -> Boolean
  Direction = (1,1,1)
  Length = 13
  Length2 = 100
  Profile = -> Sketch022
  Type = 0
FEATURE [PartDesign::Body] Body004  label="Handle"
  Group = -> [Sketch018,Pad002,Sketch019,Pocket007,Fillet,Boolean,Sketch022,Pad003]
  Origin = -> Origin004
  Tip = -> Pad003
